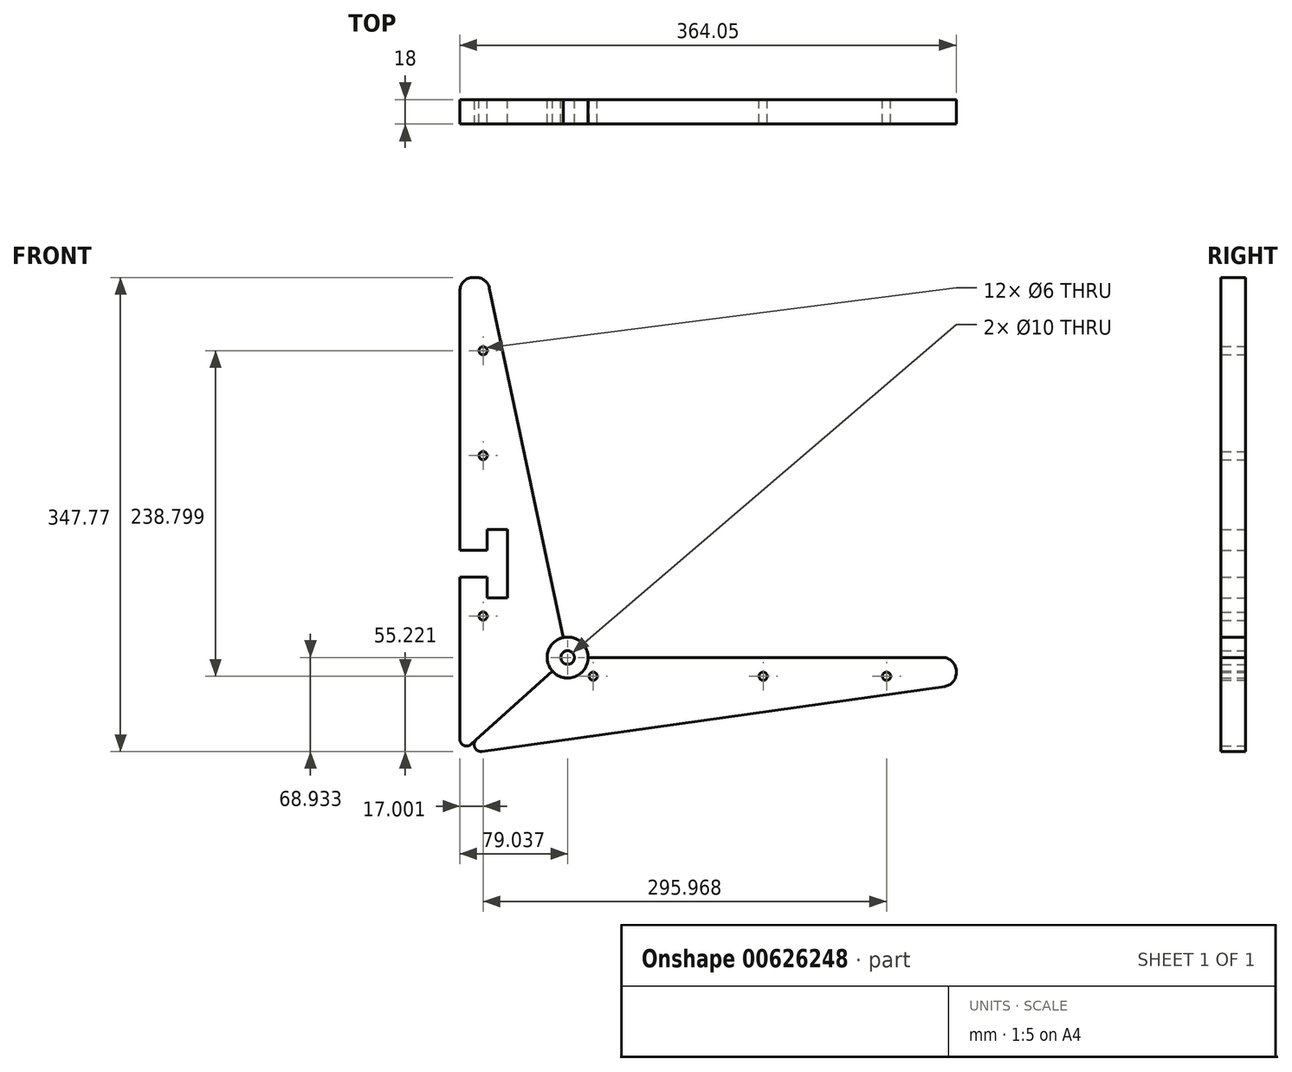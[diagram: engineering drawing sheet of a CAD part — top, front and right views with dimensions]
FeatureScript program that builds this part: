
annotation { "Feature Type Name" : "Feature", "Feature Type Description" : "" }
export const myFeature = defineFeature(function(context is Context, id is Id, definition is map)
    precondition{}
    {
        {
            var Q0;
            Q0=qCreatedBy(makeId("Front.planeOp"),FACE);
            var sketch = newSketch(context, id + "F0", { "sketchPlane" : qUnion([Q0])});
            skLineSegment(sketch, "E0", {"start": v(-60.72, 286.66) * mm, "end": v(-60.72, -63.34) * mm, "construction": true});
            skLineSegment(sketch, "E1", {"start": v(-60.72, -63.34) * mm, "end": v(299.28, -63.34) * mm, "construction": true});
            skLineSegment(sketch, "E2", {"start": v(-60.72, -63.34) * mm, "end": v(-60.72, 286.66) * mm});
            skLineSegment(sketch, "E3", {"start": v(-60.72, 286.66) * mm, "end": v(-40.72, 286.66) * mm});
            skLineSegment(sketch, "E4", {"start": v(-40.72, 286.66) * mm, "end": v(18.32, 7.82) * mm});
            skLineSegment(sketch, "E5", {"start": v(18.32, 7.82) * mm, "end": v(303.33, 7.82) * mm});
            skLineSegment(sketch, "E6", {"start": v(303.33, 7.82) * mm, "end": v(303.33, -12.18) * mm});
            skLineSegment(sketch, "E7", {"start": v(303.33, -12.18) * mm, "end": v(-60.72, -63.34) * mm});
            skLineSegment(sketch, "E8", {"start": v(18.32, 7.82) * mm, "end": v(-60.72, -63.34) * mm});
            skCircle(sketch, "E9", {"center": v(18.32, 7.82) * mm, "radius": 15 * mm});
            skCircle(sketch, "E10", {"center": v(18.32, 7.82) * mm, "radius": 5 * mm});
            skLineSegment(sketch, "E11", {"start": v(-60.72, 86.66) * mm, "end": v(-40.72, 86.66) * mm});
            skLineSegment(sketch, "E12", {"start": v(-40.72, 86.66) * mm, "end": v(-40.72, 101.66) * mm});
            skLineSegment(sketch, "E13", {"start": v(-40.72, 101.66) * mm, "end": v(-25.72, 101.66) * mm});
            skLineSegment(sketch, "E14", {"start": v(-25.72, 101.66) * mm, "end": v(-25.72, 51.66) * mm});
            skLineSegment(sketch, "E15", {"start": v(-25.72, 51.66) * mm, "end": v(-40.72, 51.66) * mm});
            skLineSegment(sketch, "E16", {"start": v(-40.72, 51.66) * mm, "end": v(-40.72, 66.66) * mm});
            skLineSegment(sketch, "E17", {"start": v(-40.72, 66.66) * mm, "end": v(-60.72, 66.66) * mm});
            skCircle(sketch, "E18", {"center": v(-43.72, 232.91) * mm, "radius": 3 * mm});
            skCircle(sketch, "E19", {"center": v(-43.72, 155.94) * mm, "radius": 3 * mm});
            skCircle(sketch, "E20", {"center": v(-43.72, 38.22) * mm, "radius": 3 * mm});
            skCircle(sketch, "E21", {"center": v(252.25, -5.89) * mm, "radius": 3 * mm});
            skCircle(sketch, "E22", {"center": v(161.73, -5.89) * mm, "radius": 3 * mm});
            skCircle(sketch, "E23", {"center": v(37.05, -5.89) * mm, "radius": 3 * mm});
            skLineSegment(sketch, "E24", {"start": v(299.28, -63.34) * mm, "end": v(299.28, 60.36) * mm, "construction": true});
            skSolve(sketch);
        }
        {
            var Q0;
            {var subQ1=sQuery(id+"F0.wireOp",EDGE,"E2");Q0=makeQuery(id+"F0.imprint","IMPRINT",FACE,{"disambiguationData":[TD([[makeQuery(id+"F0.imprint","IMPRINT",EDGE,{"derivedFrom":subQ1}),-1.0]])]});}
            extrude(context, id + "F1", {"entities" : qUnion([Q0]), "depth" : 18 * mm, "offsetDistance" : 25 * mm});
        }
        {
            var Q0;
            {var subQ1=sQuery(id+"F0.wireOp",EDGE,"E6");Q0=makeQuery(id+"F0.imprint","IMPRINT",FACE,{"disambiguationData":[TD([[makeQuery(id+"F0.imprint","IMPRINT",EDGE,{"derivedFrom":subQ1}),-1.0]])]});}
            var Q1;
            {var subQ0=sQuery(id+"F0.wireOp",EDGE,"E9");var subQ1=sQuery(id+"F0.wireOp",EDGE,"E5");var subQ2=makeQuery(id+"F0.imprint","INTERSECT",VERTEX,{"derivedFrom":[subQ1,subQ0]});Q1=makeQuery(id+"F0.imprint","IMPRINT",FACE,{"disambiguationData":[TD([[makeQuery(id+"F0.imprint","IMPRINT",EDGE,{"disambiguationData":[TD([[subQ2,1.0]])],"derivedFrom":subQ1}),-1.0]])]});}
            var Q2;
            {var subQ0=sQuery(id+"F0.wireOp",EDGE,"E9");var subQ1=sQuery(id+"F0.wireOp",EDGE,"E4");var subQ2=makeQuery(id+"F0.imprint","INTERSECT",VERTEX,{"derivedFrom":[subQ1,subQ0]});Q2=makeQuery(id+"F0.imprint","IMPRINT",FACE,{"disambiguationData":[TD([[makeQuery(id+"F0.imprint","IMPRINT",EDGE,{"disambiguationData":[TD([[subQ2,-1.0]])],"derivedFrom":subQ1}),-1.0]])]});}
            var Q3;
            {var subQ0=sQuery(id+"F0.wireOp",EDGE,"E9");var subQ1=sQuery(id+"F0.wireOp",EDGE,"E4");var subQ2=makeQuery(id+"F0.imprint","INTERSECT",VERTEX,{"derivedFrom":[subQ1,subQ0]});Q3=makeQuery(id+"F0.imprint","IMPRINT",FACE,{"disambiguationData":[TD([[makeQuery(id+"F0.imprint","IMPRINT",EDGE,{"disambiguationData":[TD([[subQ2,-1.0]])],"derivedFrom":subQ1}),1.0]])]});}
            extrude(context, id + "F2", {"entities" : qUnion([Q0, Q1, Q2, Q3]), "depth" : 18 * mm, "offsetDistance" : 25 * mm});
        }
        {
            var Q0;
            {var subQ1=sQuery(id+"F0.wireOp",EDGE,"E2");Q0=makeQuery(id+"F0.imprint","IMPRINT",FACE,{"disambiguationData":[TD([[makeQuery(id+"F0.imprint","IMPRINT",EDGE,{"derivedFrom":subQ1}),-1.0]])]});}
            var Q1;
            {var subQ0=sQuery(id+"F0.wireOp",EDGE,"E9");var subQ1=sQuery(id+"F0.wireOp",EDGE,"E4");var subQ2=makeQuery(id+"F0.imprint","INTERSECT",VERTEX,{"derivedFrom":[subQ1,subQ0]});Q1=makeQuery(id+"F0.imprint","IMPRINT",FACE,{"disambiguationData":[TD([[makeQuery(id+"F0.imprint","IMPRINT",EDGE,{"disambiguationData":[TD([[subQ2,-1.0]])],"derivedFrom":subQ1}),-1.0]])]});}
            var Q2;
            {var subQ0=sQuery(id+"F0.wireOp",EDGE,"E9");var subQ1=sQuery(id+"F0.wireOp",EDGE,"E4");var subQ2=makeQuery(id+"F0.imprint","INTERSECT",VERTEX,{"derivedFrom":[subQ1,subQ0]});Q2=makeQuery(id+"F0.imprint","IMPRINT",FACE,{"disambiguationData":[TD([[makeQuery(id+"F0.imprint","IMPRINT",EDGE,{"disambiguationData":[TD([[subQ2,-1.0]])],"derivedFrom":subQ1}),1.0]])]});}
            var Q3;
            {var subQ0=sQuery(id+"F0.wireOp",EDGE,"E9");var subQ1=sQuery(id+"F0.wireOp",EDGE,"E5");var subQ2=makeQuery(id+"F0.imprint","INTERSECT",VERTEX,{"derivedFrom":[subQ1,subQ0]});Q3=makeQuery(id+"F0.imprint","IMPRINT",FACE,{"disambiguationData":[TD([[makeQuery(id+"F0.imprint","IMPRINT",EDGE,{"disambiguationData":[TD([[subQ2,1.0]])],"derivedFrom":subQ1}),-1.0]])]});}
            extrude(context, id + "F3", {"entities" : qUnion([Q0, Q1, Q2, Q3]), "depth" : 18 * mm, "offsetDistance" : 25 * mm});
        }
        {
            var Q0;
            {var subQ1=sQuery(id+"F0.wireOp",EDGE,"E6");Q0=makeQuery(id+"F0.imprint","IMPRINT",FACE,{"disambiguationData":[TD([[makeQuery(id+"F0.imprint","IMPRINT",EDGE,{"derivedFrom":subQ1}),-1.0]])]});}
            extrude(context, id + "F4", {"entities" : qUnion([Q0]), "depth" : 18 * mm, "offsetDistance" : 25 * mm});
        }
        {
            var Q0;
            Q0=makeQuery(id+"F2.opExtrude","SWEPT_EDGE",EDGE,{"disambiguationData":[OSD([sQuery(id+"F0.wireOp",EDGE,"E2"),sQuery(id+"F0.wireOp",EDGE,"E7"),sQuery(id+"F0.wireOp",EDGE,"E8")])]});
            var Q1;
            Q1=makeQuery(id+"F1.opExtrude","SWEPT_EDGE",EDGE,{"disambiguationData":[OSD([sQuery(id+"F0.wireOp",EDGE,"E2"),sQuery(id+"F0.wireOp",EDGE,"E7"),sQuery(id+"F0.wireOp",EDGE,"E8")])]});
            var Q2;
            Q2=makeQuery(id+"F3.opExtrude","SWEPT_EDGE",EDGE,{"disambiguationData":[OSD([sQuery(id+"F0.wireOp",EDGE,"E2"),sQuery(id+"F0.wireOp",EDGE,"E7"),sQuery(id+"F0.wireOp",EDGE,"E8")])]});
            var Q3;
            Q3=makeQuery(id+"F4.opExtrude","SWEPT_EDGE",EDGE,{"disambiguationData":[OSD([sQuery(id+"F0.wireOp",EDGE,"E2"),sQuery(id+"F0.wireOp",EDGE,"E7"),sQuery(id+"F0.wireOp",EDGE,"E8")])]});
            fillet(context, id + "F5", {"entities" : qUnion([Q0, Q1, Q2, Q3]), "radius" : 5 * mm, "tangentPropagation" : true, "allowEdgeOverflow" : false});
        }
        {
            var Q0;
            Q0=makeQuery(id+"F4.opExtrude","SWEPT_EDGE",EDGE,{"disambiguationData":[OSD([sQuery(id+"F0.wireOp",EDGE,"E5"),sQuery(id+"F0.wireOp",EDGE,"E6")])]});
            var Q1;
            Q1=makeQuery(id+"F4.opExtrude","SWEPT_EDGE",EDGE,{"disambiguationData":[OSD([sQuery(id+"F0.wireOp",EDGE,"E6"),sQuery(id+"F0.wireOp",EDGE,"E7")])]});
            var Q2;
            Q2=makeQuery(id+"F3.opExtrude","SWEPT_EDGE",EDGE,{"disambiguationData":[OSD([sQuery(id+"F0.wireOp",EDGE,"E2"),sQuery(id+"F0.wireOp",EDGE,"E3")])]});
            var Q3;
            Q3=makeQuery(id+"F3.opExtrude","SWEPT_EDGE",EDGE,{"disambiguationData":[OSD([sQuery(id+"F0.wireOp",EDGE,"E3"),sQuery(id+"F0.wireOp",EDGE,"E4")])]});
            var Q4;
            Q4=makeQuery(id+"F1.opExtrude","SWEPT_EDGE",EDGE,{"disambiguationData":[OSD([sQuery(id+"F0.wireOp",EDGE,"E2"),sQuery(id+"F0.wireOp",EDGE,"E3")])]});
            var Q5;
            Q5=makeQuery(id+"F1.opExtrude","SWEPT_EDGE",EDGE,{"disambiguationData":[OSD([sQuery(id+"F0.wireOp",EDGE,"E3"),sQuery(id+"F0.wireOp",EDGE,"E4")])]});
            var Q6;
            Q6=makeQuery(id+"F2.opExtrude","SWEPT_EDGE",EDGE,{"disambiguationData":[OSD([sQuery(id+"F0.wireOp",EDGE,"E5"),sQuery(id+"F0.wireOp",EDGE,"E6")])]});
            var Q7;
            Q7=makeQuery(id+"F2.opExtrude","SWEPT_EDGE",EDGE,{"disambiguationData":[OSD([sQuery(id+"F0.wireOp",EDGE,"E6"),sQuery(id+"F0.wireOp",EDGE,"E7")])]});
            fillet(context, id + "F6", {"entities" : qUnion([Q0, Q1, Q2, Q3, Q4, Q5, Q6, Q7]), "radius" : 10 * mm, "tangentPropagation" : true, "allowEdgeOverflow" : false});
        }
    });
